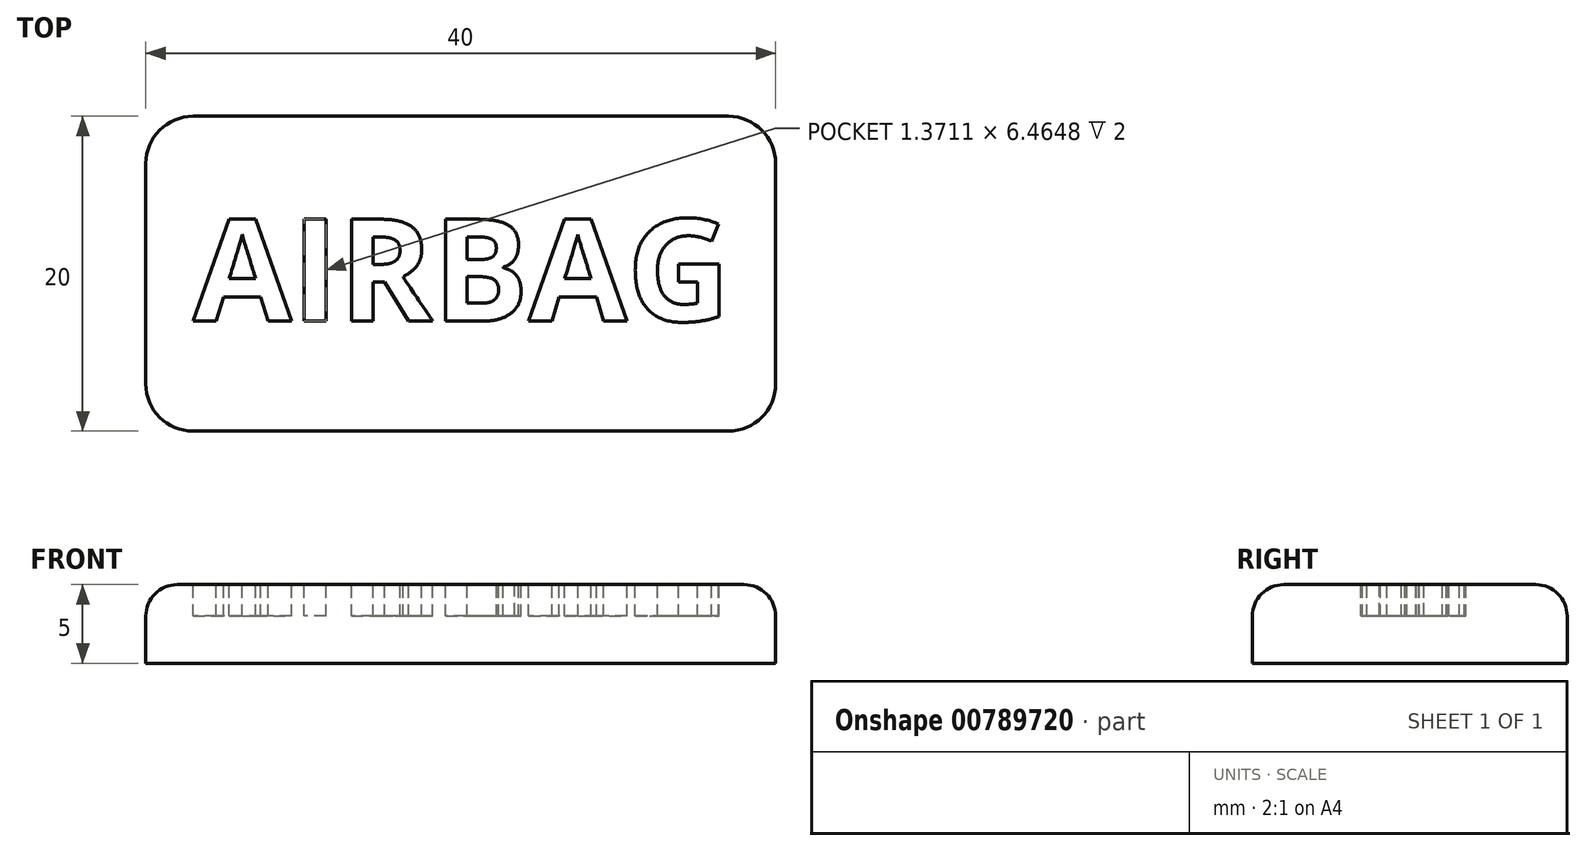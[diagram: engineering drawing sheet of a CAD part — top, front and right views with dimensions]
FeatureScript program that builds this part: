
annotation { "Feature Type Name" : "Feature", "Feature Type Description" : "" }
export const myFeature = defineFeature(function(context is Context, id is Id, definition is map)
    precondition{}
    {
        {
            var Q0;
            Q0=qCreatedBy(makeId("Top.planeOp"),FACE);
            var sketch = newSketch(context, id + "F0", { "sketchPlane" : qUnion([Q0])});
            skLineSegment(sketch, "E0.bottom", {"start": v(-16.81, 8.8) * mm, "end": v(17.19, 8.8) * mm});
            skLineSegment(sketch, "E0.top", {"start": v(-16.81, -11.2) * mm, "end": v(17.19, -11.2) * mm});
            skLineSegment(sketch, "E0.left", {"start": v(-19.81, 5.8) * mm, "end": v(-19.81, -8.2) * mm});
            skLineSegment(sketch, "E0.right", {"start": v(20.19, 5.8) * mm, "end": v(20.19, -8.2) * mm});
            skPoint(sketch, "E1.visualSharp", {"position": v(-19.81, 8.8) * mm});
            skArc(sketch, "E1.filletArc", {"start": v(-16.81, 8.8) * mm, "mid": v(-18.94, 7.93) * mm, "end": v(-19.81, 5.8) * mm});
            skPoint(sketch, "E2.visualSharp", {"position": v(20.19, 8.8) * mm});
            skArc(sketch, "E2.filletArc", {"start": v(20.19, 5.8) * mm, "mid": v(19.3, 7.93) * mm, "end": v(17.19, 8.8) * mm});
            skPoint(sketch, "E3.visualSharp", {"position": v(-19.81, -11.2) * mm});
            skArc(sketch, "E3.filletArc", {"start": v(-19.81, -8.2) * mm, "mid": v(-18.94, -10.32) * mm, "end": v(-16.81, -11.2) * mm});
            skPoint(sketch, "E4.visualSharp", {"position": v(20.19, -11.2) * mm});
            skArc(sketch, "E4.filletArc", {"start": v(17.19, -11.2) * mm, "mid": v(19.3, -10.32) * mm, "end": v(20.19, -8.2) * mm});
            skText(sketch, "E5", { "text": "AIRBAG", "fontName": "OpenSans-Regular.ttf"});
            const initialGuessF0  = {"E5": [-0.01431, -0.0041, 1, 0, 0.00591]};
            skSetInitialGuess(sketch, initialGuessF0);
            skSolve(sketch);
        }
        {
            var Q0;
            Q0 = qSketchRegion(id + "F0", true);
            var Q1;
            Q1=makeQuery(id+"F0.imprint","IMPRINT",FACE,{"disambiguationData":[TD([[makeQuery(id+"F0.imprint","IMPRINT",EDGE,{"derivedFrom":sQuery(id+"F0.wireOp",EDGE,"E5.sketch_text.stroke-8")}),1.0]])]});
            var Q2;
            Q2=makeQuery(id+"F0.imprint","IMPRINT",FACE,{"disambiguationData":[TD([[makeQuery(id+"F0.imprint","IMPRINT",EDGE,{"derivedFrom":sQuery(id+"F0.wireOp",EDGE,"E5.sketch_text.stroke-13")}),-1.0]])]});
            var Q3;
            Q3=makeQuery(id+"F0.imprint","IMPRINT",FACE,{"disambiguationData":[TD([[makeQuery(id+"F0.imprint","IMPRINT",EDGE,{"derivedFrom":sQuery(id+"F0.wireOp",EDGE,"E5.sketch_text.stroke-28")}),1.0]])]});
            var Q4;
            Q4=makeQuery(id+"F0.imprint","IMPRINT",FACE,{"disambiguationData":[TD([[makeQuery(id+"F0.imprint","IMPRINT",EDGE,{"derivedFrom":sQuery(id+"F0.wireOp",EDGE,"E5.sketch_text.stroke-53")}),1.0]])]});
            var Q5;
            Q5=makeQuery(id+"F0.imprint","IMPRINT",FACE,{"disambiguationData":[TD([[makeQuery(id+"F0.imprint","IMPRINT",EDGE,{"derivedFrom":sQuery(id+"F0.wireOp",EDGE,"E5.sketch_text.stroke-68")}),1.0]])]});
            var Q6;
            Q6=makeQuery(id+"F0.imprint","IMPRINT",FACE,{"disambiguationData":[TD([[makeQuery(id+"F0.imprint","IMPRINT",EDGE,{"derivedFrom":sQuery(id+"F0.wireOp",EDGE,"E5.sketch_text.stroke-73")}),-1.0]])]});
            var Q7;
            Q7=makeQuery(id+"F0.imprint","IMPRINT",FACE,{"disambiguationData":[TD([[makeQuery(id+"F0.imprint","IMPRINT",EDGE,{"derivedFrom":sQuery(id+"F0.wireOp",EDGE,"E5.sketch_text.stroke-0")}),-1.0]])]});
            var Q8;
            Q8=makeQuery(id+"F0.imprint","IMPRINT",FACE,{"disambiguationData":[TD([[makeQuery(id+"F0.imprint","IMPRINT",EDGE,{"derivedFrom":sQuery(id+"F0.wireOp",EDGE,"E5.sketch_text.stroke-17")}),-1.0]])]});
            var Q9;
            Q9=makeQuery(id+"F0.imprint","IMPRINT",FACE,{"disambiguationData":[TD([[makeQuery(id+"F0.imprint","IMPRINT",EDGE,{"derivedFrom":sQuery(id+"F0.wireOp",EDGE,"E5.sketch_text.stroke-60")}),-1.0]])]});
            var Q10;
            Q10=makeQuery(id+"F0.imprint","IMPRINT",FACE,{"disambiguationData":[TD([[makeQuery(id+"F0.imprint","IMPRINT",EDGE,{"derivedFrom":sQuery(id+"F0.wireOp",EDGE,"E5.sketch_text.stroke-35")}),-1.0]])]});
            var Q11;
            Q11=makeQuery(id+"F0.imprint","IMPRINT",FACE,{"disambiguationData":[TD([[makeQuery(id+"F0.imprint","IMPRINT",EDGE,{"derivedFrom":sQuery(id+"F0.wireOp",EDGE,"E0.bottom")}),-1.0]])]});
            var Q12;
            Q12=makeQuery(id+"F0.imprint","IMPRINT",FACE,{"disambiguationData":[TD([[makeQuery(id+"F0.imprint","IMPRINT",EDGE,{"derivedFrom":sQuery(id+"F0.wireOp",EDGE,"E5.sketch_text.stroke-46")}),1.0]])]});
            extrude(context, id + "F1", {"entities" : qUnion([Q0, Q1, Q2, Q3, Q4, Q5, Q6, Q7, Q8, Q9, Q10, Q11, Q12]), "depth" : 5 * mm, "offsetDistance" : 25 * mm});
        }
        {
            var Q0;
            Q0=makeQuery(id+"F1.opExtrude","CAP_FACE",FACE,{"disambiguationData":[OSD([sQuery(id+"F0.wireOp",EDGE,"E0.bottom"),sQuery(id+"F0.wireOp",EDGE,"E0.top"),sQuery(id+"F0.wireOp",EDGE,"E0.left"),sQuery(id+"F0.wireOp",EDGE,"E0.right"),sQuery(id+"F0.wireOp",EDGE,"E1.filletArc"),sQuery(id+"F0.wireOp",EDGE,"E2.filletArc"),sQuery(id+"F0.wireOp",EDGE,"E3.filletArc"),sQuery(id+"F0.wireOp",EDGE,"E4.filletArc")])],"isStart":false});
            var sketch = newSketch(context, id + "F2", { "sketchPlane" : qUnion([Q0])});
            skText(sketch, "E6", { "text": "AIRBAG", "fontName": "OpenSans-Bold.ttf"});
            const initialGuessF2  = {"E6": [-0.01681, -0.0042, 1, 0, 0.00652]};
            skSetInitialGuess(sketch, initialGuessF2);
            skSolve(sketch);
        }
        {
            var Q0;
            Q0 = qSketchRegion(id + "F2", true);
            extrude(context, id + "F3", {"entities" : qUnion([Q0]), "operationType" : NewBodyOperationType.REMOVE, "oppositeDirection" : true, "depth" : 2 * mm, "offsetDistance" : 25 * mm});
        }
        {
            var Q0;
            Q0=makeQuery(id+"F1.opExtrude","CAP_EDGE",EDGE,{"disambiguationData":[OSD([sQuery(id+"F0.wireOp",EDGE,"E0.left")])],"isStart":false});
            var Q1;
            Q1=makeQuery(id+"F1.opExtrude","CAP_EDGE",EDGE,{"disambiguationData":[OSD([sQuery(id+"F0.wireOp",EDGE,"E3.filletArc")])],"isStart":false});
            var Q2;
            Q2=makeQuery(id+"F1.opExtrude","CAP_EDGE",EDGE,{"disambiguationData":[OSD([sQuery(id+"F0.wireOp",EDGE,"E0.top")])],"isStart":false});
            var Q3;
            Q3=makeQuery(id+"F1.opExtrude","CAP_EDGE",EDGE,{"disambiguationData":[OSD([sQuery(id+"F0.wireOp",EDGE,"E4.filletArc")])],"isStart":false});
            var Q4;
            Q4=makeQuery(id+"F1.opExtrude","CAP_EDGE",EDGE,{"disambiguationData":[OSD([sQuery(id+"F0.wireOp",EDGE,"E0.right")])],"isStart":false});
            var Q5;
            Q5=makeQuery(id+"F1.opExtrude","CAP_EDGE",EDGE,{"disambiguationData":[OSD([sQuery(id+"F0.wireOp",EDGE,"E2.filletArc")])],"isStart":false});
            var Q6;
            Q6=makeQuery(id+"F1.opExtrude","CAP_EDGE",EDGE,{"disambiguationData":[OSD([sQuery(id+"F0.wireOp",EDGE,"E0.bottom")])],"isStart":false});
            var Q7;
            Q7=makeQuery(id+"F1.opExtrude","CAP_EDGE",EDGE,{"disambiguationData":[OSD([sQuery(id+"F0.wireOp",EDGE,"E1.filletArc")])],"isStart":false});
            fillet(context, id + "F4", {"entities" : qUnion([Q0, Q1, Q2, Q3, Q4, Q5, Q6, Q7]), "radius" : 2 * mm, "tangentPropagation" : true, "allowEdgeOverflow" : false});
        }
    });
